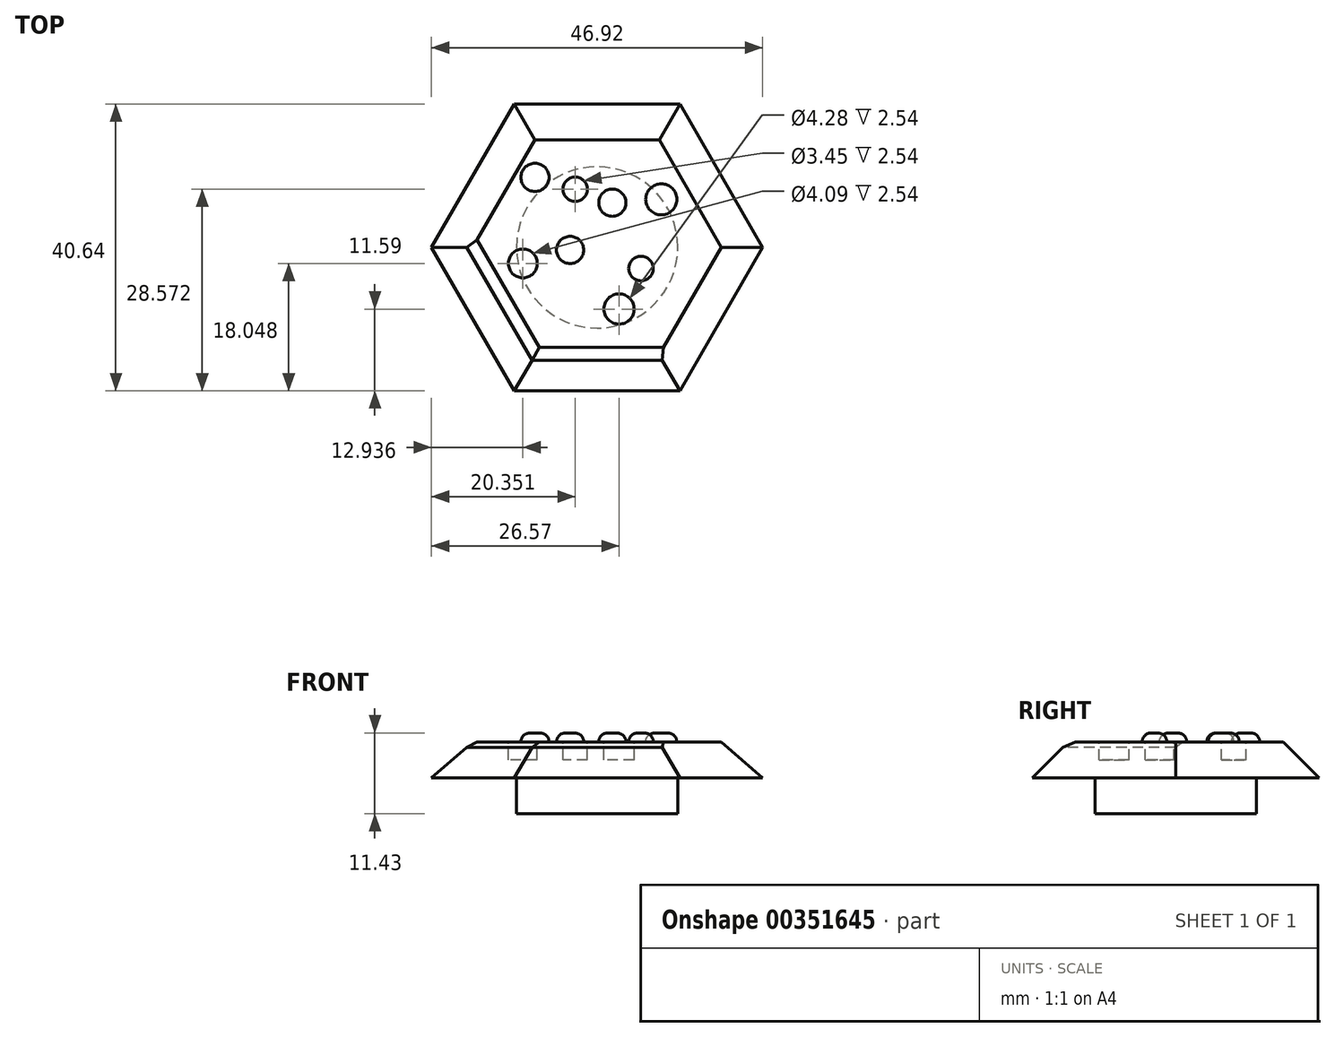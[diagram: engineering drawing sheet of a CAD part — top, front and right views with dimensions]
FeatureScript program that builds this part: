
annotation { "Feature Type Name" : "Feature", "Feature Type Description" : "" }
export const myFeature = defineFeature(function(context is Context, id is Id, definition is map)
    precondition{}
    {
        {
            var Q0;
            Q0=qCreatedBy(makeId("Top.planeOp"),FACE);
            var sketch = newSketch(context, id + "F0", { "sketchPlane" : qUnion([Q0])});
            skCircle(sketch, "E0", {"center": v(0, 0) * mm, "radius": 11.43 * mm});
            skSolve(sketch);
        }
        {
            var Q0;
            Q0 = qSketchRegion(id + "F0", true);
            extrude(context, id + "F1", {"entities" : qUnion([Q0]), "depth" : 5.08 * mm});
        }
        {
            var Q0;
            Q0=makeQuery(id+"F1.opExtrude","CAP_FACE",FACE,{"disambiguationData":[OSD([sQuery(id+"F0.wireOp",EDGE,"E0")])],"isStart":false});
            var sketch = newSketch(context, id + "F2", { "sketchPlane" : qUnion([Q0])});
            skCircle(sketch, "E1.cCircle", {"center": v(0, 0) * mm, "radius": 23.46 * mm, "construction": true});
            skLineSegment(sketch, "E1.0", {"start": v(23.46, 0) * mm, "end": v(11.73, -20.32) * mm});
            skLineSegment(sketch, "E1.1", {"start": v(11.73, -20.32) * mm, "end": v(-11.73, -20.32) * mm});
            skLineSegment(sketch, "E1.2", {"start": v(-11.73, -20.32) * mm, "end": v(-23.46, 0) * mm});
            skLineSegment(sketch, "E1.3", {"start": v(-23.46, 0) * mm, "end": v(-11.73, 20.32) * mm});
            skLineSegment(sketch, "E1.4", {"start": v(-11.73, 20.32) * mm, "end": v(11.73, 20.32) * mm});
            skLineSegment(sketch, "E1.5", {"start": v(11.73, 20.32) * mm, "end": v(23.46, 0) * mm});
            skSolve(sketch);
        }
        {
            var Q0;
            Q0 = qSketchRegion(id + "F2", true);
            extrude(context, id + "F3", {"entities" : qUnion([Q0]), "operationType" : NewBodyOperationType.ADD, "depth" : 5.08 * mm});
        }
        {
            var Q0;
            Q0=makeQuery(id+"F3.opExtrude","CAP_EDGE",EDGE,{"disambiguationData":[OSD([sQuery(id+"F2.wireOp",EDGE,"E1.1")])],"isStart":false});
            var Q1;
            Q1=makeQuery(id+"F3.opExtrude","CAP_EDGE",EDGE,{"disambiguationData":[OSD([sQuery(id+"F2.wireOp",EDGE,"E1.0")])],"isStart":false});
            var Q2;
            Q2=makeQuery(id+"F3.opExtrude","CAP_EDGE",EDGE,{"disambiguationData":[OSD([sQuery(id+"F2.wireOp",EDGE,"E1.2")])],"isStart":false});
            var Q3;
            Q3=makeQuery(id+"F3.opExtrude","CAP_EDGE",EDGE,{"disambiguationData":[OSD([sQuery(id+"F2.wireOp",EDGE,"E1.3")])],"isStart":false});
            var Q4;
            Q4=makeQuery(id+"F3.opExtrude","CAP_EDGE",EDGE,{"disambiguationData":[OSD([sQuery(id+"F2.wireOp",EDGE,"E1.4")])],"isStart":false});
            var Q5;
            Q5=makeQuery(id+"F3.opExtrude","CAP_EDGE",EDGE,{"disambiguationData":[OSD([sQuery(id+"F2.wireOp",EDGE,"E1.5")])],"isStart":false});
            chamfer(context, id + "F4", {"entities" : qUnion([Q0, Q1, Q2, Q3, Q4, Q5]), "width" : 5.08 * mm, "tangentPropagation" : true});
        }
        {
            var Q0;
            Q0=makeQuery(id+"F3.opExtrude","CAP_FACE",FACE,{"disambiguationData":[OSD([sQuery(id+"F2.wireOp",EDGE,"E1.0"),sQuery(id+"F2.wireOp",EDGE,"E1.1"),sQuery(id+"F2.wireOp",EDGE,"E1.2"),sQuery(id+"F2.wireOp",EDGE,"E1.3"),sQuery(id+"F2.wireOp",EDGE,"E1.4"),sQuery(id+"F2.wireOp",EDGE,"E1.5")])],"isStart":false});
            var sketch = newSketch(context, id + "F5", { "sketchPlane" : qUnion([Q0])});
            skCircle(sketch, "E2", {"center": v(-8.8, 9.93) * mm, "radius": 2 * mm});
            skCircle(sketch, "E3", {"center": v(9.09, 6.82) * mm, "radius": 2.2 * mm});
            skCircle(sketch, "E4", {"center": v(6.22, -2.99) * mm, "radius": 1.74 * mm});
            skCircle(sketch, "E5", {"center": v(-3.83, -0.36) * mm, "radius": 1.93 * mm});
            skCircle(sketch, "E6", {"center": v(2.15, 6.34) * mm, "radius": 1.93 * mm});
            skEllipse(sketch, "E7", {"center": v(0, -8.01) * mm, "majorRadius": 5.5 * mm, "minorRadius": 1.14 * mm, "majorAxis": v(1, -0.04)});
            skSolve(sketch);
        }
        {
            var Q0;
            Q0=makeQuery(id+"F5.imprint","IMPRINT",FACE,{"disambiguationData":[TD([[makeQuery(id+"F5.imprint","IMPRINT",EDGE,{"derivedFrom":sQuery(id+"F5.wireOp",EDGE,"E2")}),1.0]])]});
            var Q1;
            Q1=makeQuery(id+"F5.imprint","IMPRINT",FACE,{"disambiguationData":[TD([[makeQuery(id+"F5.imprint","IMPRINT",EDGE,{"derivedFrom":sQuery(id+"F5.wireOp",EDGE,"E3")}),1.0]])]});
            var Q2;
            Q2=makeQuery(id+"F5.imprint","IMPRINT",FACE,{"disambiguationData":[TD([[makeQuery(id+"F5.imprint","IMPRINT",EDGE,{"derivedFrom":sQuery(id+"F5.wireOp",EDGE,"E4")}),1.0]])]});
            var Q3;
            Q3=makeQuery(id+"F5.imprint","IMPRINT",FACE,{"disambiguationData":[TD([[makeQuery(id+"F5.imprint","IMPRINT",EDGE,{"derivedFrom":sQuery(id+"F5.wireOp",EDGE,"E5")}),1.0]])]});
            var Q4;
            Q4=makeQuery(id+"F5.imprint","IMPRINT",FACE,{"disambiguationData":[TD([[makeQuery(id+"F5.imprint","IMPRINT",EDGE,{"derivedFrom":sQuery(id+"F5.wireOp",EDGE,"E6")}),1.0]])]});
            var Q5;
            {var subQ0=sQuery(id+"F5.wireOp",EDGE,"E7");var subQ1=sQuery(id+"F5.wireOp",EDGE,"vNfGp6NR-0M3B-6KPb-Q8hn-rwX3kNQlag7t");var subQ2=makeQuery(id+"F5.imprint","INTERSECT",VERTEX,{"disambiguationData":[OD(0.0)],"derivedFrom":[subQ1,subQ0]});Q5=makeQuery(id+"F5.imprint","IMPRINT",FACE,{"disambiguationData":[TD([[makeQuery(id+"F5.imprint","IMPRINT",EDGE,{"disambiguationData":[TD([[subQ2,-1.0]])],"derivedFrom":subQ1}),1.0]])]});}
            var Q6;
            {var subQ0=sQuery(id+"F5.wireOp",EDGE,"E7");var subQ1=sQuery(id+"F5.wireOp",EDGE,"vNfGp6NR-0M3B-6KPb-Q8hn-rwX3kNQlag7t");var subQ2=makeQuery(id+"F5.imprint","INTERSECT",VERTEX,{"disambiguationData":[OD(0.0)],"derivedFrom":[subQ1,subQ0]});Q6=makeQuery(id+"F5.imprint","IMPRINT",FACE,{"disambiguationData":[TD([[makeQuery(id+"F5.imprint","IMPRINT",EDGE,{"disambiguationData":[TD([[subQ2,-1.0]])],"derivedFrom":subQ1}),-1.0]])]});}
            var Q7;
            Q7=makeQuery(id+"F5.imprint","IMPRINT",FACE,{"disambiguationData":[TD([[makeQuery(id+"F5.imprint","IMPRINT",EDGE,{"derivedFrom":sQuery(id+"F5.wireOp",EDGE,"E2")}),1.0]])]});
            var Q8;
            {var subQ0=sQuery(id+"F5.wireOp",EDGE,"E7");var subQ1=sQuery(id+"F5.wireOp",EDGE,"vNfGp6NR-0M3B-6KPb-Q8hn-rwX3kNQlag7t");var subQ2=makeQuery(id+"F5.imprint","INTERSECT",VERTEX,{"disambiguationData":[OD(0.0)],"derivedFrom":[subQ1,subQ0]});Q8=makeQuery(id+"F5.imprint","IMPRINT",FACE,{"disambiguationData":[TD([[makeQuery(id+"F5.imprint","IMPRINT",EDGE,{"disambiguationData":[TD([[subQ2,1.0]])],"derivedFrom":subQ1}),1.0]])]});}
            extrude(context, id + "F6", {"entities" : qUnion([Q0, Q1, Q2, Q3, Q4, Q5, Q6, Q7, Q8]), "operationType" : NewBodyOperationType.ADD, "depth" : 1.27 * mm});
        }
        {
            var Q0;
            Q0=makeQuery(id+"F6.opExtrude","CAP_EDGE",EDGE,{"disambiguationData":[OSD([sQuery(id+"F5.wireOp",EDGE,"E5")])],"isStart":false});
            var Q1;
            Q1=makeQuery(id+"F6.opExtrude","CAP_EDGE",EDGE,{"disambiguationData":[OSD([sQuery(id+"F5.wireOp",EDGE,"E2")])],"isStart":false});
            var Q2;
            Q2=makeQuery(id+"F6.opExtrude","CAP_EDGE",EDGE,{"disambiguationData":[OSD([sQuery(id+"F5.wireOp",EDGE,"E6")])],"isStart":false});
            var Q3;
            Q3=makeQuery(id+"F6.opExtrude","CAP_EDGE",EDGE,{"disambiguationData":[OSD([sQuery(id+"F5.wireOp",EDGE,"E3")])],"isStart":false});
            var Q4;
            Q4=makeQuery(id+"F6.opExtrude","CAP_EDGE",EDGE,{"disambiguationData":[OSD([sQuery(id+"F5.wireOp",EDGE,"E4")])],"isStart":false});
            fillet(context, id + "F7", {"entities" : qUnion([Q0, Q1, Q2, Q3, Q4]), "radius" : 1.27 * mm, "tangentPropagation" : true, "allowEdgeOverflow" : false});
        }
        {
            var Q0;
            Q0=makeQuery(id+"F3.opExtrude","CAP_FACE",FACE,{"disambiguationData":[OSD([sQuery(id+"F2.wireOp",EDGE,"E1.0"),sQuery(id+"F2.wireOp",EDGE,"E1.1"),sQuery(id+"F2.wireOp",EDGE,"E1.2"),sQuery(id+"F2.wireOp",EDGE,"E1.3"),sQuery(id+"F2.wireOp",EDGE,"E1.4"),sQuery(id+"F2.wireOp",EDGE,"E1.5")])],"isStart":false});
            var sketch = newSketch(context, id + "F8", { "sketchPlane" : qUnion([Q0])});
            skCircle(sketch, "E8", {"center": v(-10.52, -2.27) * mm, "radius": 2.04 * mm});
            skCircle(sketch, "E9", {"center": v(3.1, -8.73) * mm, "radius": 2.14 * mm});
            skCircle(sketch, "E10", {"center": v(-3.1, 8.25) * mm, "radius": 1.72 * mm});
            skSolve(sketch);
        }
        {
            var Q0;
            Q0=makeQuery(id+"F8.imprint","IMPRINT",FACE,{"disambiguationData":[TD([[makeQuery(id+"F8.imprint","IMPRINT",EDGE,{"derivedFrom":sQuery(id+"F8.wireOp",EDGE,"E8")}),1.0]])]});
            var Q1;
            Q1=makeQuery(id+"F8.imprint","IMPRINT",FACE,{"disambiguationData":[TD([[makeQuery(id+"F8.imprint","IMPRINT",EDGE,{"derivedFrom":sQuery(id+"F8.wireOp",EDGE,"E10")}),1.0]])]});
            var Q2;
            Q2=makeQuery(id+"F8.imprint","IMPRINT",FACE,{"disambiguationData":[TD([[makeQuery(id+"F8.imprint","IMPRINT",EDGE,{"derivedFrom":sQuery(id+"F8.wireOp",EDGE,"E9")}),1.0]])]});
            extrude(context, id + "F9", {"entities" : qUnion([Q0, Q1, Q2]), "operationType" : NewBodyOperationType.REMOVE, "oppositeDirection" : true, "depth" : 2.54 * mm});
        }
        {
            var Q0;
            Q0=makeQuery(id+"F9.boolean.opBoolean","COPY",EDGE,{"derivedFrom":makeQuery(id+"F9.opExtrude","CAP_EDGE",EDGE,{"disambiguationData":[OSD([sQuery(id+"F8.wireOp",EDGE,"E8")])],"isStart":true})});
            var Q1;
            Q1=makeQuery(id+"F9.boolean.opBoolean","COPY",EDGE,{"derivedFrom":makeQuery(id+"F9.opExtrude","CAP_EDGE",EDGE,{"disambiguationData":[OSD([sQuery(id+"F8.wireOp",EDGE,"E10")])],"isStart":true})});
            var Q2;
            Q2=makeQuery(id+"F9.boolean.opBoolean","COPY",EDGE,{"derivedFrom":makeQuery(id+"F9.opExtrude","CAP_EDGE",EDGE,{"disambiguationData":[OSD([sQuery(id+"F8.wireOp",EDGE,"E9")])],"isStart":true})});
            var Q3;
            {var subQ0=sQuery(id+"F2.wireOp",EDGE,"E1.2");Q3=makeQuery(id+"F4.opChamfer","BLEND_EDGE",EDGE,{"blendedFrom":[makeQuery(id+"F3.opExtrude","CAP_EDGE",EDGE,{"disambiguationData":[OSD([subQ0])],"isStart":false}),makeQuery(id+"F3.opExtrude","CAP_FACE",FACE,{"disambiguationData":[OSD([sQuery(id+"F2.wireOp",EDGE,"E1.0"),sQuery(id+"F2.wireOp",EDGE,"E1.1"),subQ0,sQuery(id+"F2.wireOp",EDGE,"E1.3"),sQuery(id+"F2.wireOp",EDGE,"E1.4"),sQuery(id+"F2.wireOp",EDGE,"E1.5")])],"isStart":false})],"blendedInto":[makeQuery(id+"F3.opExtrude","CAP_FACE",FACE,{"disambiguationData":[OSD([sQuery(id+"F2.wireOp",EDGE,"E1.0"),sQuery(id+"F2.wireOp",EDGE,"E1.1"),subQ0,sQuery(id+"F2.wireOp",EDGE,"E1.3"),sQuery(id+"F2.wireOp",EDGE,"E1.4"),sQuery(id+"F2.wireOp",EDGE,"E1.5")])],"isStart":false})]});}
            var Q4;
            {var subQ0=sQuery(id+"F2.wireOp",EDGE,"E1.1");Q4=makeQuery(id+"F4.opChamfer","BLEND_EDGE",EDGE,{"blendedFrom":[makeQuery(id+"F3.opExtrude","CAP_EDGE",EDGE,{"disambiguationData":[OSD([subQ0])],"isStart":false}),makeQuery(id+"F3.opExtrude","CAP_FACE",FACE,{"disambiguationData":[OSD([sQuery(id+"F2.wireOp",EDGE,"E1.0"),subQ0,sQuery(id+"F2.wireOp",EDGE,"E1.2"),sQuery(id+"F2.wireOp",EDGE,"E1.3"),sQuery(id+"F2.wireOp",EDGE,"E1.4"),sQuery(id+"F2.wireOp",EDGE,"E1.5")])],"isStart":false})],"blendedInto":[makeQuery(id+"F3.opExtrude","CAP_FACE",FACE,{"disambiguationData":[OSD([sQuery(id+"F2.wireOp",EDGE,"E1.0"),subQ0,sQuery(id+"F2.wireOp",EDGE,"E1.2"),sQuery(id+"F2.wireOp",EDGE,"E1.3"),sQuery(id+"F2.wireOp",EDGE,"E1.4"),sQuery(id+"F2.wireOp",EDGE,"E1.5")])],"isStart":false})]});}
            chamfer(context, id + "F10", {"entities" : qUnion([Q0, Q1, Q2, Q3, Q4]), "width" : 2.54 * mm, "tangentPropagation" : true});
        }
    });
